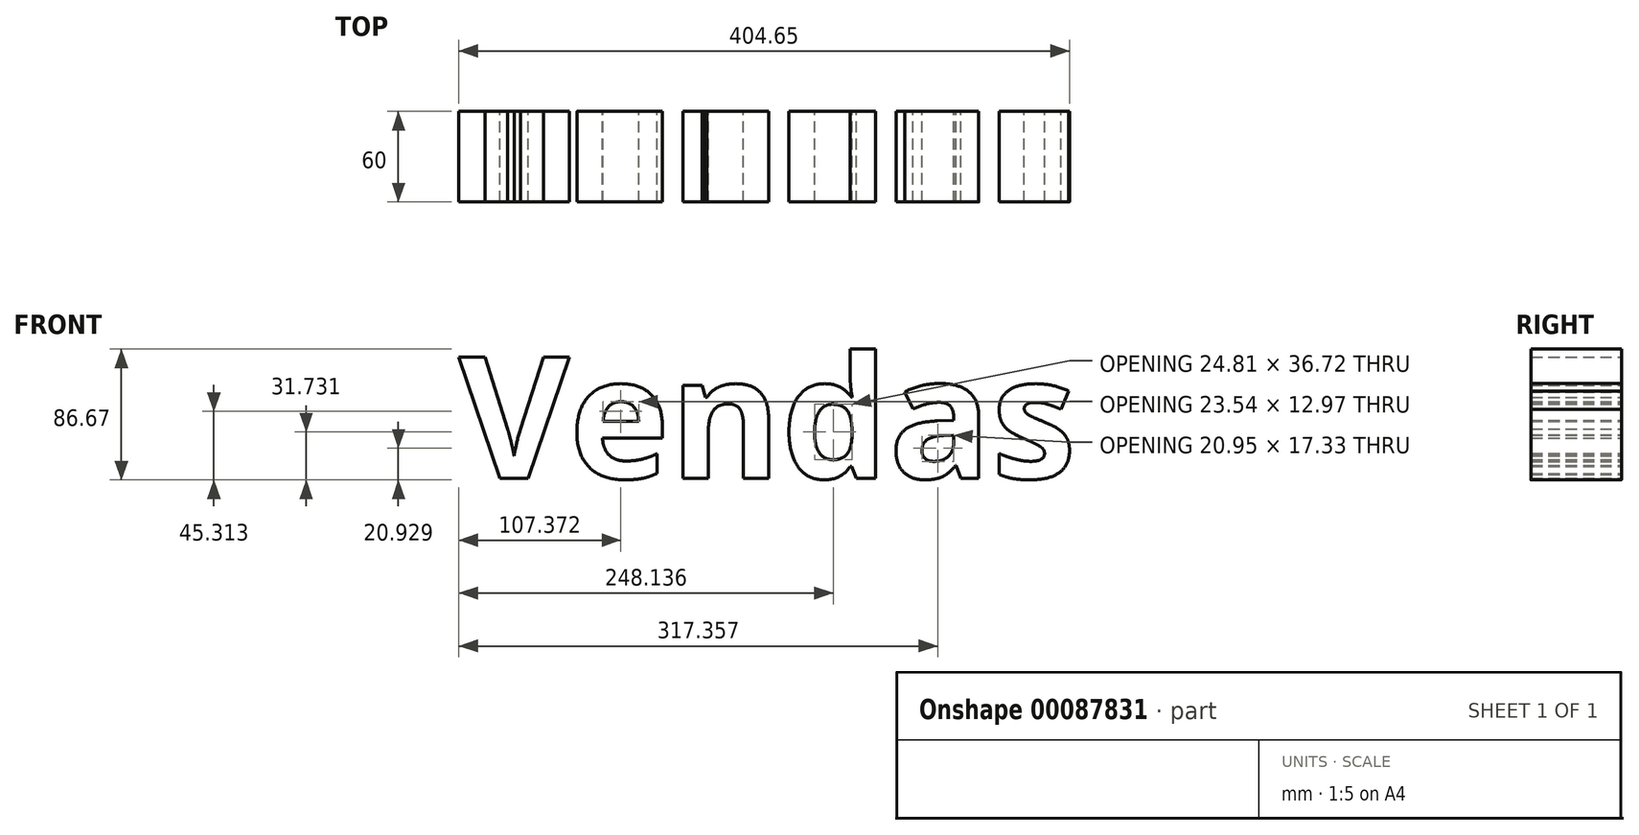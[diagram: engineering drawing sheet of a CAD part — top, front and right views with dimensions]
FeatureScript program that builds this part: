
annotation { "Feature Type Name" : "Feature", "Feature Type Description" : "" }
export const myFeature = defineFeature(function(context is Context, id is Id, definition is map)
    precondition{}
    {
        {
            var Q0;
            Q0=qCreatedBy(makeId("Front.planeOp"),FACE);
            var sketch = newSketch(context, id + "F0", { "sketchPlane" : qUnion([Q0])});
            skText(sketch, "E0", { "text": "Vendas", "fontName": "OpenSans-Bold.ttf"});
            const initialGuessF0  = {"E0": [-0.19266, 0.04925, 1, 0, 0.08107]};
            skSetInitialGuess(sketch, initialGuessF0);
            skSolve(sketch);
        }
        {
            var Q0;
            Q0 = qSketchRegion(id + "F0", true);
            extrude(context, id + "F1", {"entities" : qUnion([Q0]), "endBound" : BoundingType.SYMMETRIC, "depth" : 60 * mm});
        }
    });
